# Revit family: PD9-FP types Avec hôte
name_source: partatom
category: Dispositifs d'éclairage
units: mm (PartAtom-declared; Revit-internal decimal feet)

## family parameters
Conserver l'orientation des annotations = Oui
Cote de connecteur circulaire = Utiliser le diamètre
Couper avec des vides une fois chargée = Non
Hôte = Face
Partagée = Non
Point de calcul de pièce = Non
Type d'élément = Normal

## types (14) — shared parameters
Code d'assemblage = D5010200
Fabricant = B.E.G.
Hauteur de montage max = 300 cm
Image du type = 360°.jpg
Marque = LUXOMAT
Mode de pose = Faux Plafond
URL = http://www.luxomat.com
zero-valued in all types: Elévation par défaut

## per-type parameters (varying)
| type | Alimentation | Charge Cos ɸ =0.5 | Charge Cos ɸ =1 | Charge LED | Classe | Commentaires du type | Consommation | IP | Modèle | Relais | Référence | Température ambiante | Type de Sortie |
| 01- PD9-FP Générique | 110-240 V AC |  |  |  | II | MINI.DET.PRES.360°/Ø10M FAUX PLAFOND |  | 20 | PD9-FP |  |  | -25°C à +50°C |  |
| 02- PD9-1C-FP réf 92902 | 110-240 V AC | 500 VA | 1000 W | 200 W | II | MINI.DET.MOUV.1 CONTACT.360°/Ø10M FAUX PLAFOND | 0,40 W | 20 | PD9-1C-FP | 4,3 A | 92902 | -25°C à +50°C | TOR |
| 14- PD9-1C-12-48V-FP réf 92985 | 12-48 V AC/DC | 1150 VA | 2300 W | 300 W | II | MINI.DET.MOUV.12-48V.1 CONTACT.360°/Ø10M FAUX PLAFOND | 0,40 W | 20 | PD9-1C-12-48V-FP | 10 A | 92985 | -25°C à +50°C | TOR |
| 03- PD9-M-1C-FP réf 92900 | 110-240 V AC | 1150 VA | 2300 W | 300 W | II | MINI.DET.PRES.MAITRE.1 CONTACT.360°/Ø10M FAUX PLAFOND | 0,40 W | 20 | PD9-M-1C-FP | 10 A | 92900 | -25°C à +50°C | TOR |
| 04- PD9-M-1C-IP65-FP réf 92912 | 110-240 V AC | 1150 VA | 2300 W | 300 W | Alim. II / Tête III | MINI.DET.PRES.SALLE DE BAIN.MAITRE.1 CONTACT.360°/Ø10M FAUX PLAFOND | 1 W | Alim. 20 / Tête 65 | PD9-M-1C-IP65-FP | 10 A | 92912 | -25°C à +50°C | TOR |
| 05- PD9-M-2C-FP réf 92976 | 110-240 V AC | 1150 VA | 2300 W | 300 W | II | MINI.DET.PRES.MAITRE.2 CONTACTS.360°/Ø10M FAUX PLAFOND | 0,45 W | 20 | PD9-M-2C-FP | 10 A / 3 A | 92976 | -25°C à +50°C | TOR + CVC |
| 07- PD9-M-DIM-FP réf 92910 | 110-240 V AC | 1150 VA | 2300 W | 300 W | II | MINI.DET.PRES.MAITRE.DIM(1-10V).360°/Ø10M FAUX PLAFOND | 0,47 W | 20 | PD9-M-DIM-FP | 10 A | 92910 | -25°C à +50°C | DIM (50 ballasts maxi) |
| 08- PD9-M-DIM-CVC-FP réf 92973 | 110-240 V AC | 1150 VA | 2300 W | 300 W | II | MINI.DET.PRES.MAITRE.DIM(1-10V) + CVC.360°/Ø10M FAUX PLAFOND | 0,50 W | 23 | PD9-M-DIM-CVC-FP | 10 A / 3 A | 92973 | -25°C à +50°C | DIM (50 ballasts maxi) + CVC |
| 06- PD9N-M-DACO-FP réf 93470 | 110-240 V AC | 0 | 0 | 0 | II | MINI.DET.PRES.MAITRE.DALI 2.360°/Ø10M FAUX PLAFOND | 2 W | 20 | PD9N-M-DACO-FP | 0 | 93470 | -25°C à +50°C | DALI 2  (40 drivers maxi) |
| 11- PD9N-KNX-DX-FP réf 93390 | 24 V DC par Bus KNX | 0 | 0 | 0 | II | MINI.DET.PRES.KNX.VERSION DELUXE.360°/Ø10M FAUX PLAFOND | 12 mA | 20 | PD9N-KNX-DX-FP | 0 | 93390 | -5°C à +45°C | KNX - 1 sortie Eclairage TOR ou GRADATION / 3 sorties Présence / Capteur de température |
| 13- PD9N-LON-FP réf 92989 | 24 V DC par Bus LON | 0 | 0 | 0 | II | MINI.DET.PRES.LON.360°/Ø10M FAUX PLAFOND | 12 mA | 20 | PD9N-LON-FP | 0 | 92989 | +5°C à +50°C | LON |
| 09- PD9-S-FP réf 92905 | 110-240 V AC | 0 | 0 | 0 | II | MINI.DET.PRES.ESCLAVE.360°/Ø10M FAUX PLAFOND | 0,25 W | 20 | PD9-S-FP | 0 | 92905 | -25°C à +50°C | Esclave |
| 10- PD9-S-IP65-FP réf 92915 | 110-240 V AC | 0 | 0 | 0 | Tête III | MINI.DET.PRES.SALLE DE BAIN.ESCLAVE.360°/Ø10M FAUX PLAFOND | 0,25 W | Tête 65 | PD9-S-IP65-FP | 0 | 92915 | -25°C à +50°C | Esclave |
| 12- PD9N-KNXs-DX-FP réf 93520 | 24 V DC par Bus KNX | 0 | 0 | 0 | II | MINI.DET.PRES.KNX Secure.VERSION DELUXE.360°/Ø10M FAUX PLAFOND | 12 mA | 20 | PD9N-KNXs-DX-FP | 0 | 93520 | -5°C à +45°C | KNX Sécure - 1 sortie Eclairage TOR ou GRADATION / 3 sorties Présence |
